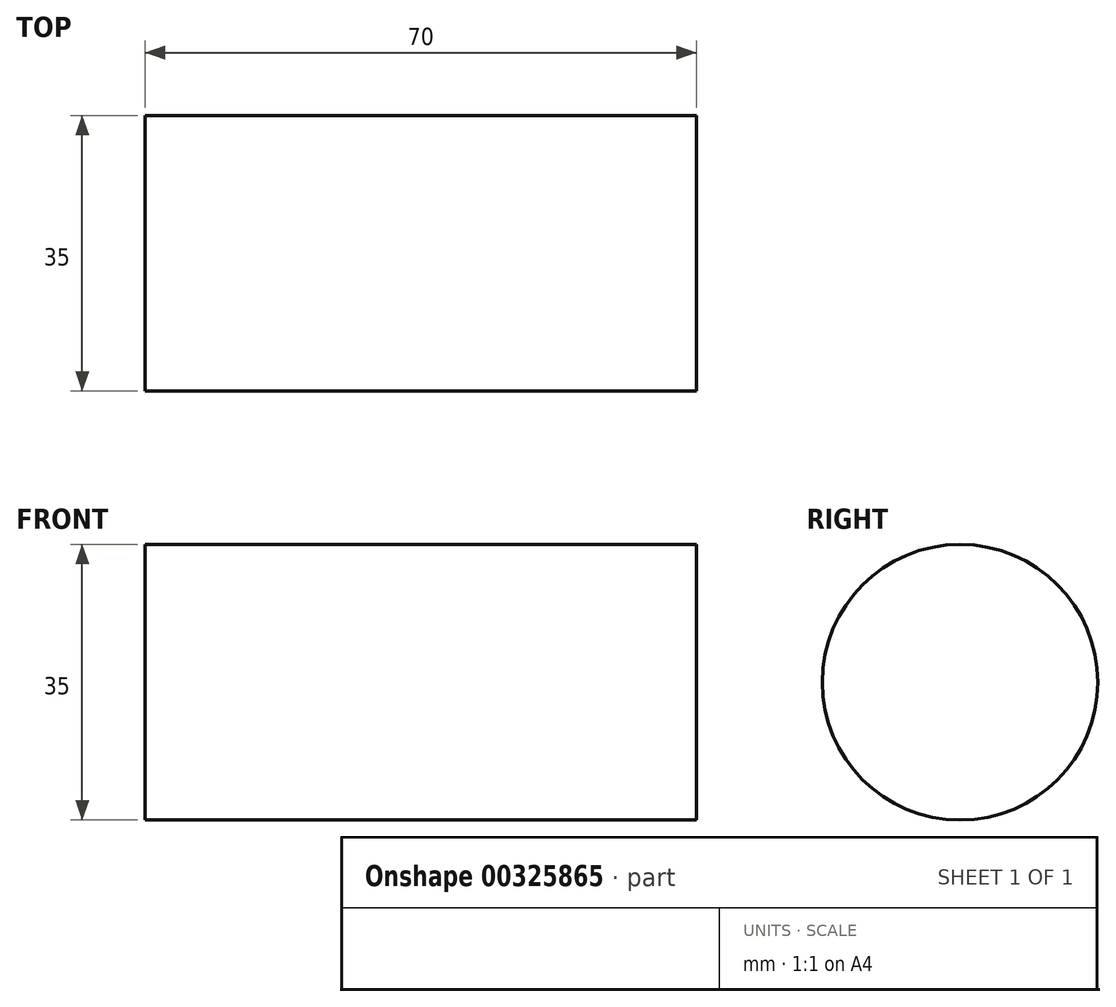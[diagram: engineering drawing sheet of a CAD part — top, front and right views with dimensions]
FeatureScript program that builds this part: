
annotation { "Feature Type Name" : "Feature", "Feature Type Description" : "" }
export const myFeature = defineFeature(function(context is Context, id is Id, definition is map)
    precondition{}
    {
        {
            var Q0;
            Q0=qCreatedBy(makeId("Right.planeOp"),FACE);
            var sketch = newSketch(context, id + "F0", { "sketchPlane" : qUnion([Q0])});
            skCircle(sketch, "E0", {"center": v(0, 0) * mm, "radius": 17.5 * mm});
            skSolve(sketch);
        }
        {
            var Q0;
            Q0=makeQuery(id+"F0.imprint","IMPRINT",FACE,{"disambiguationData":[TD([[makeQuery(id+"F0.imprint","IMPRINT",EDGE,{"derivedFrom":sQuery(id+"F0.wireOp",EDGE,"E0")}),1.0]])]});
            extrude(context, id + "F1", {"entities" : qUnion([Q0]), "depth" : 70 * mm});
        }
    });
